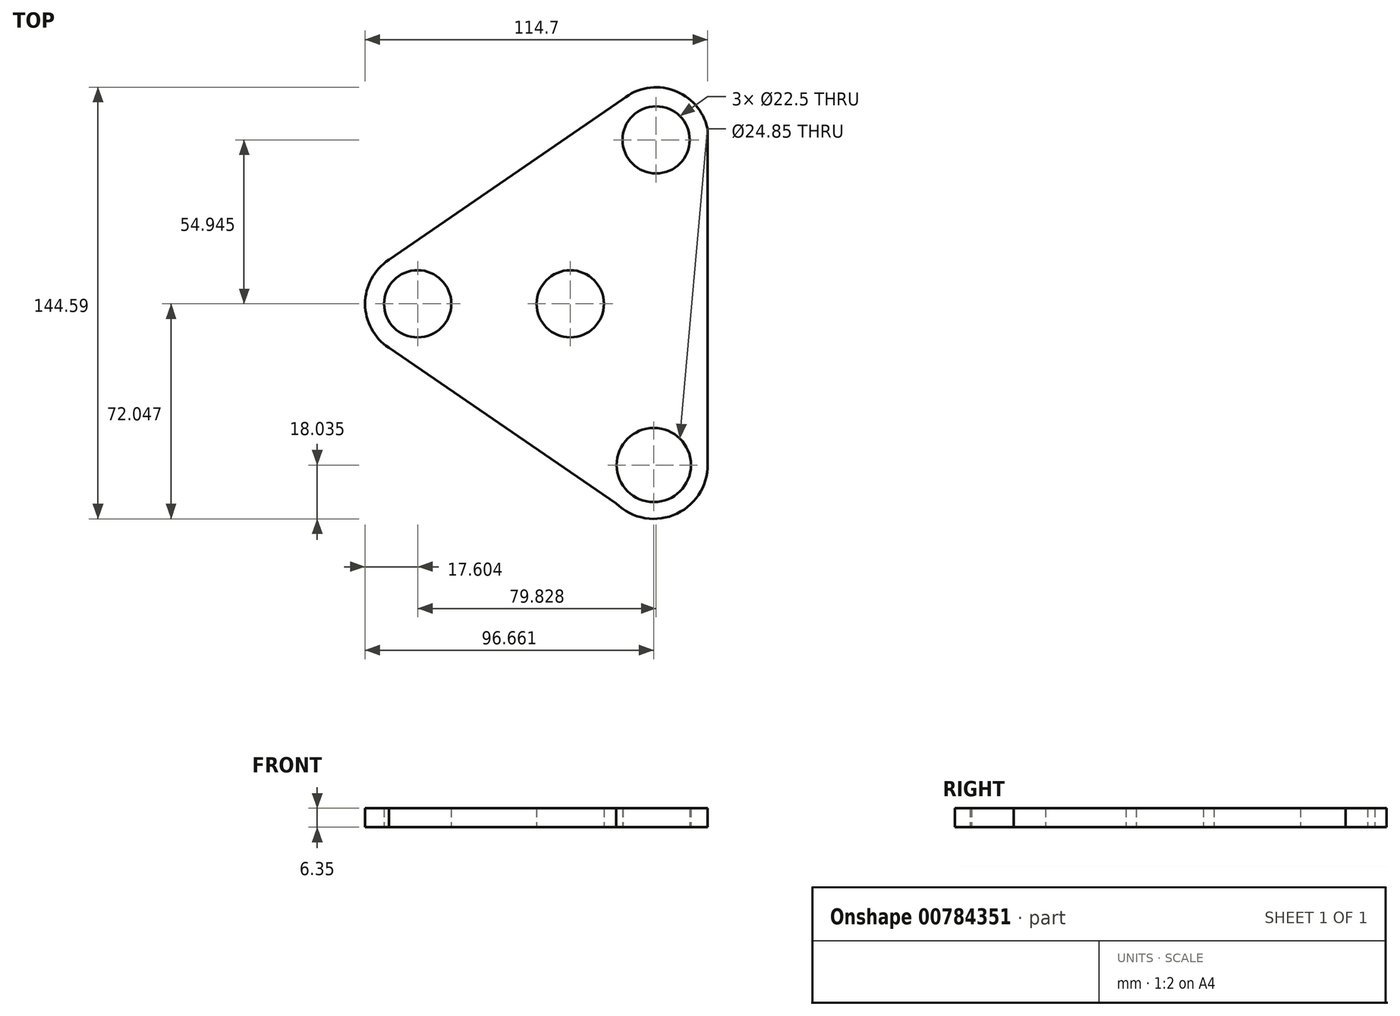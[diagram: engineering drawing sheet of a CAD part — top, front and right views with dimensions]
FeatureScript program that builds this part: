
annotation { "Feature Type Name" : "Feature", "Feature Type Description" : "" }
export const myFeature = defineFeature(function(context is Context, id is Id, definition is map)
    precondition{}
    {
        {
            var Q0;
            Q0=qCreatedBy(makeId("Top.planeOp"),FACE);
            var sketch = newSketch(context, id + "F0", { "sketchPlane" : qUnion([Q0])});
            skCircle(sketch, "E0", {"center": v(-85.6, -46.28) * mm, "radius": 12.43 * mm});
            skCircle(sketch, "E1", {"center": v(-84.84, 62.67) * mm, "radius": 11.25 * mm});
            skCircle(sketch, "E2", {"center": v(-113.58, 7.73) * mm, "radius": 11.25 * mm});
            skCircle(sketch, "E3", {"center": v(-164.67, 7.73) * mm, "radius": 11.25 * mm});
            skPoint(sketch, "E4.center", {"position": v(0, 0) * mm});
            skArc(sketch, "E5.0", {"start": v(-67.66, 66.5) * mm, "mid": v(-79.05, 79.3) * mm, "end": v(-95.92, 76.35) * mm});
            skArc(sketch, "E6.0", {"start": v(-174.34, 22.43) * mm, "mid": v(-182.27, 7.73) * mm, "end": v(-174.34, -6.98) * mm});
            skLineSegment(sketch, "E7", {"start": v(-174.34, 22.43) * mm, "end": v(-95.92, 76.35) * mm});
            skArc(sketch, "E8.0", {"start": v(-98.23, -59.17) * mm, "mid": v(-77.83, -62.56) * mm, "end": v(-67.66, -44.55) * mm});
            skLineSegment(sketch, "E9", {"start": v(-67.66, 66.5) * mm, "end": v(-67.66, -44.55) * mm});
            skLineSegment(sketch, "E10", {"start": v(-174.34, -6.98) * mm, "end": v(-98.23, -59.17) * mm});
            skSolve(sketch);
        }
        {
            var Q0;
            Q0 = qSketchRegion(id + "F0", true);
            extrude(context, id + "F1", {"entities" : qUnion([Q0]), "depth" : 6.35 * mm, "offsetDistance" : 25.4 * mm});
        }
    });
